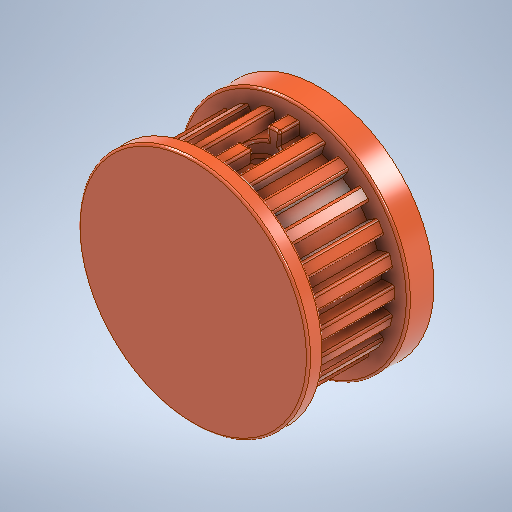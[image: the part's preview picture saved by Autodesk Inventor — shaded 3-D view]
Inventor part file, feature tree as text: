
AUTODESK INVENTOR PART (.ipt)
format: ipt  version: 2025 (Build 290162000, 162)  size: 641,024 bytes
history: native  units: mm
features: extrude x10, projected_geometry x6, sketch x5, pattern_circular x1, plane x1, fillet x1
ambient origin geometry x8: Origin, YZ Plane, XZ Plane, XY Plane, X Axis, Y Axis, Z Axis, Center Point
bodies: Solid1 (feature_tree)
feature tree (24):
  extrude  "Extrusion1"  Depth=3.0mm TaperAngle=0.0deg
  extrude  "Extrusion2"  Depth=1.6mm TaperAngle=0.0deg
  extrude  "Extrusion3"  Depth=14.772116mm
  extrude  "Extrusion4"  Depth=34.7251mm
  pattern_circular  "Circular Pattern2"  Count=24 Angle=360.0deg
  extrude  "Extrusion5"  Depth=0.4mm
  extrude  "Extrusion6"  Depth=10.0mm TaperAngle=0.0deg
  extrude  "Extrusion7"  Depth=10.0mm
  extrude  "Extrusion11"  Depth=10.0mm TaperAngle=0.0deg
  plane  "Work Plane1"
  extrude  "Extrusion9"  Depth=10.0mm
  extrude  "Extrusion10"  Depth=5.0mm TaperAngle=0.0deg
  fillet  "Fillet2"  Radius=0.654498mm
  sketch  "Sketch3"  dims[d0=45.0mm d1=3.0mm d2=0.0mm]
  sketch  "Sketch4"  dims[d3=41.0mm d4=1.6mm d5=0.0mm]
  sketch  "Sketch5"  dims[d6=2.0mm d7=0.0mm d11=14.772116mm]
  sketch  "Sketch6"  dims[d13=39.7251mm d14=34.7251mm]
  projected_geometry  "Projected Loop2"
  projected_geometry  "Projected Loop3"
  projected_geometry  "Projected Loop4"
  projected_geometry  "Projected Loop5"
  projected_geometry  "Projected Loop6"
  projected_geometry  "Projected Loop7"
  sketch  "Sketch11"  dims[d17=16.5mm d18=0.0mm d23=240.0mm d24=360.0deg d26=0.4mm d27=1.0mm d28=0.0mm d29=5.2mm d31=20.0mm d32=0.0mm d33=5.2mm d34=5.0mm d35=0.0mm d37=0.654498mm d38=0.654498mm d39=0.0mm d46=20.1mm d47=10.0mm d48=3.1mm d49=20.0mm d50=0.0mm d51=5.5mm d52=5.0mm d53=0.0mm d54=0.4mm d55=2.0mm d56=0.0mm d57=10.0mm d58=2.9mm d59=1.45mm]
